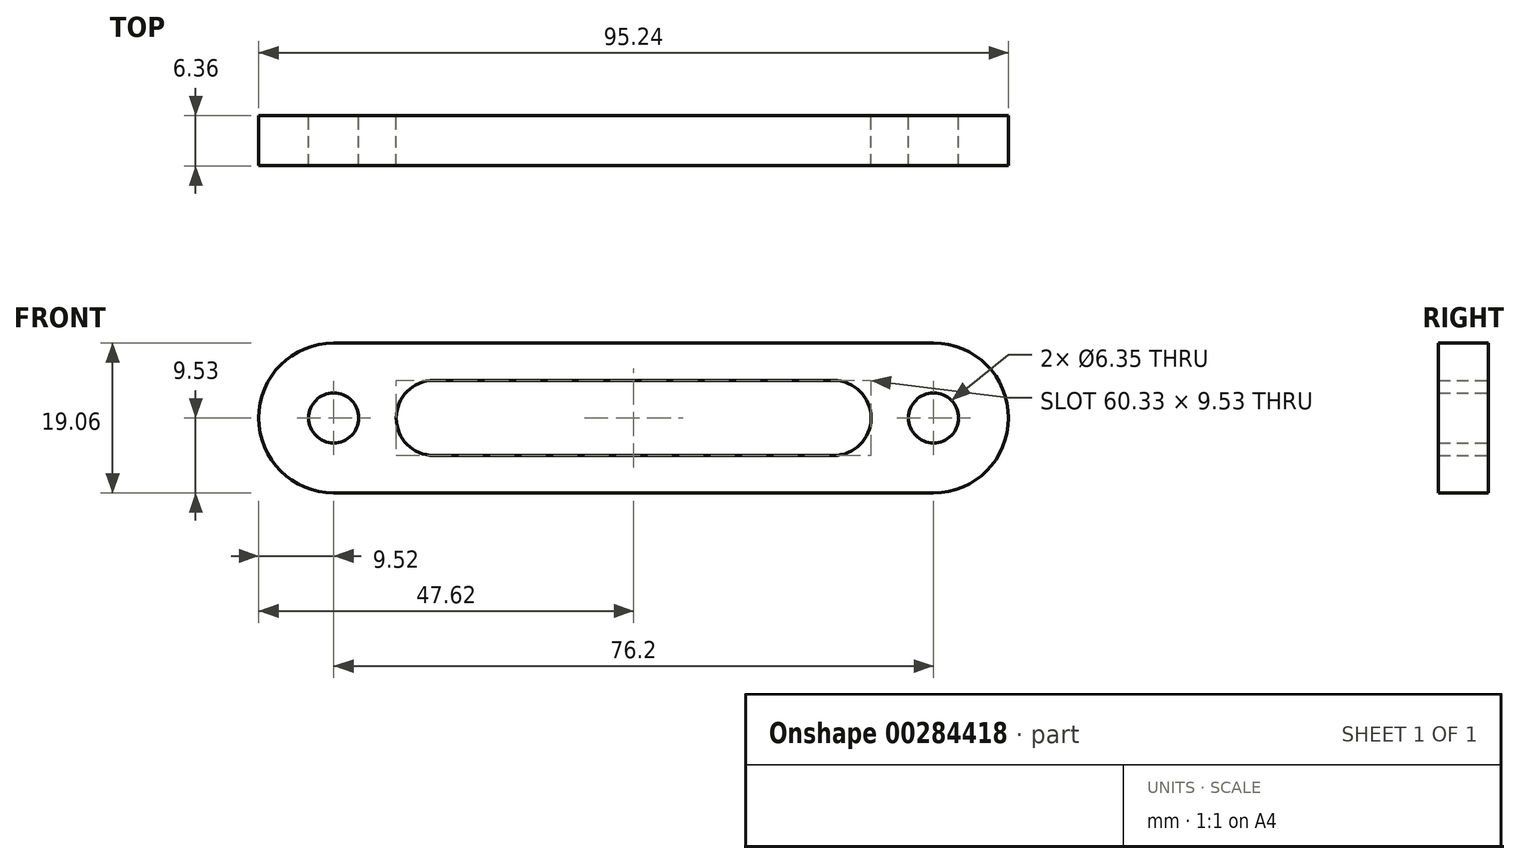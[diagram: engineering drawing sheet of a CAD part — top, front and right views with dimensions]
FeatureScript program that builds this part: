
annotation { "Feature Type Name" : "Feature", "Feature Type Description" : "" }
export const myFeature = defineFeature(function(context is Context, id is Id, definition is map)
    precondition{}
    {
        {
            var Q0;
            Q0=qCreatedBy(makeId("Front.planeOp"),FACE);
            var sketch = newSketch(context, id + "F0", { "sketchPlane" : qUnion([Q0])});
            skLineSegment(sketch, "E0.bottom", {"start": v(38.1, -9.52) * mm, "end": v(-38.1, -9.53) * mm});
            skLineSegment(sketch, "E0.top", {"start": v(38.1, 9.53) * mm, "end": v(-38.1, 9.52) * mm});
            skPoint(sketch, "E0.middle", {"position": v(0, 0) * mm});
            skLineSegment(sketch, "E1.bottom", {"start": v(25.4, -4.76) * mm, "end": v(-25.4, -4.76) * mm});
            skLineSegment(sketch, "E1.top", {"start": v(25.4, 4.76) * mm, "end": v(-25.4, 4.76) * mm});
            skArc(sketch, "E2", {"start": v(-38.1, 9.52) * mm, "mid": v(-47.62, 0) * mm, "end": v(-38.1, -9.53) * mm});
            skArc(sketch, "E3", {"start": v(38.1, -9.52) * mm, "mid": v(47.62, 0) * mm, "end": v(38.1, 9.53) * mm});
            skArc(sketch, "E4", {"start": v(-25.4, 4.76) * mm, "mid": v(-30.16, 0) * mm, "end": v(-25.4, -4.76) * mm});
            skArc(sketch, "E5", {"start": v(25.4, -4.76) * mm, "mid": v(30.16, 0) * mm, "end": v(25.4, 4.76) * mm});
            skCircle(sketch, "E6", {"center": v(-38.1, 0) * mm, "radius": 3.18 * mm});
            skCircle(sketch, "E7", {"center": v(38.1, 0) * mm, "radius": 3.18 * mm});
            skSolve(sketch);
        }
        {
            var Q0;
            Q0=makeQuery(id+"F0.imprint","IMPRINT",FACE,{"disambiguationData":[TD([[makeQuery(id+"F0.imprint","IMPRINT",EDGE,{"derivedFrom":sQuery(id+"F0.wireOp",EDGE,"E0.bottom")}),-1.0]])]});
            extrude(context, id + "F1", {"entities" : qUnion([Q0]), "depth" : 6.35 * mm, "symmetric" : true});
        }
    });
